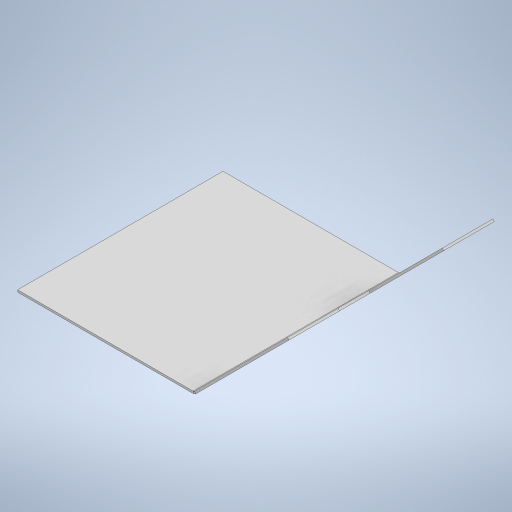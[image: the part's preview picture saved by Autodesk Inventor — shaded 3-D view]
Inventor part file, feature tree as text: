
AUTODESK INVENTOR PART (.ipt)
format: ipt  version: 2024.3 (Build 283343000, 343)  size: 279,040 bytes
history: native  units: mm
features: sheet_metal_op x4, other x4, sketch x3
ambient origin geometry x8: Origin, YZ Plane, XZ Plane, XY Plane, X Axis, Y Axis, Z Axis, Center Point
bodies: Solid1 (feature_tree)
feature tree (11):
  sheet_metal_op  "Face1"
  sheet_metal_op  "Flange1"
  sketch  "Sketch1"  dims[d0=197.0mm]
  other  "Plate1"
  sketch  "Sketch2"  dims[d1=169.946mm]
  other  "Plate2"
  sheet_metal_op  "Bend1"
  sheet_metal_op  "Corner1"
  sketch  "Sketch3"  dims[d2=2.0mm d3=2.0mm d4=1.0mm d5=4.0mm d6=2.0mm d7=127.842mm d8=45.0deg d9=2.0mm d10=8.0mm d11=2.0mm d12=2.0mm d13=100.0mm d14=100.0mm d15=48.5mm d16=2.0mm d17=0.0mm]
  other  "Cut1"
  other  "Definition1"
